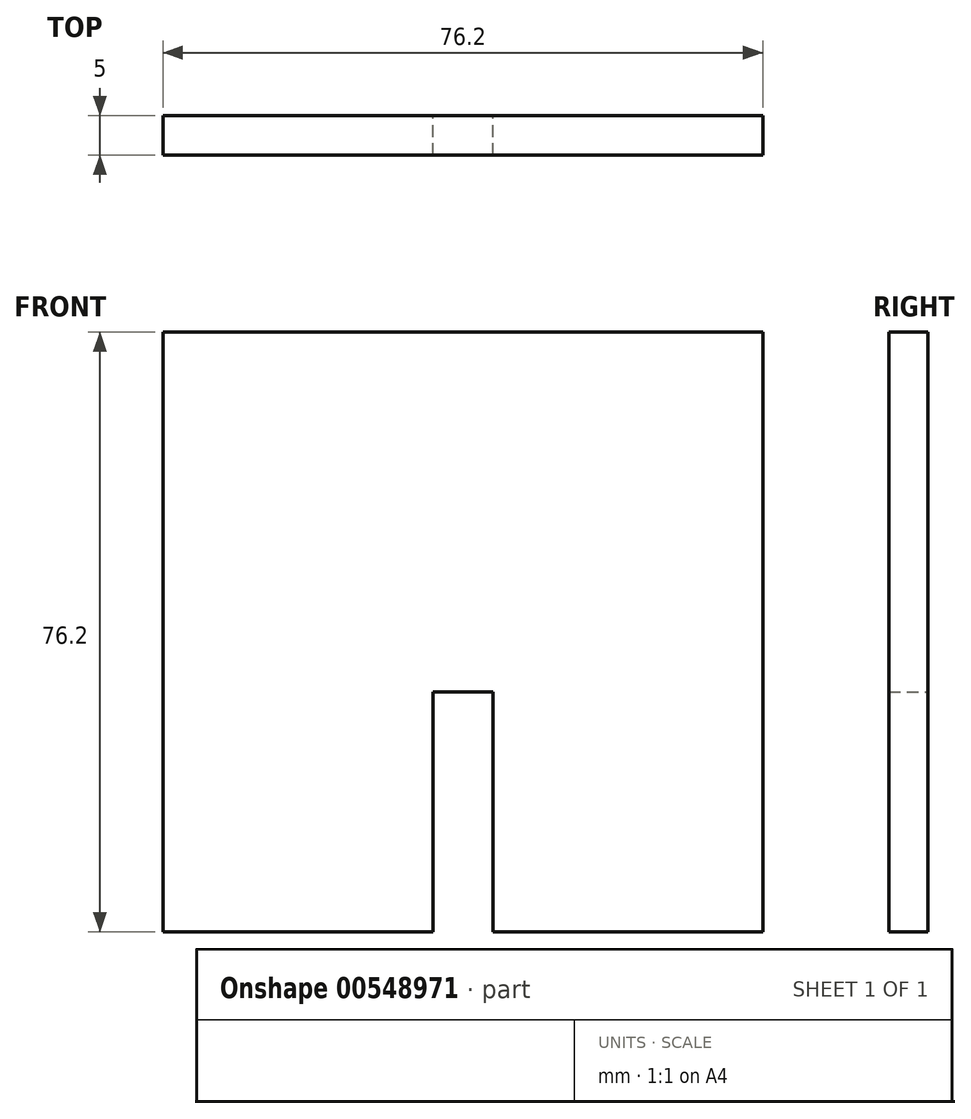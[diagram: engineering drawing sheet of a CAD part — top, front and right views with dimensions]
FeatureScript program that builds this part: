
annotation { "Feature Type Name" : "Feature", "Feature Type Description" : "" }
export const myFeature = defineFeature(function(context is Context, id is Id, definition is map)
    precondition{}
    {
        {
            var Q0;
            Q0=qCreatedBy(makeId("Front.planeOp"),FACE);
            var sketch = newSketch(context, id + "F0", { "sketchPlane" : qUnion([Q0])});
            skLineSegment(sketch, "E0.bottom", {"start": v(-11.31, -25.19) * mm, "end": v(64.89, -25.19) * mm});
            skLineSegment(sketch, "E0.top", {"start": v(-11.31, 51.01) * mm, "end": v(64.89, 51.01) * mm});
            skLineSegment(sketch, "E0.left", {"start": v(-11.31, -25.19) * mm, "end": v(-11.31, 51.01) * mm});
            skLineSegment(sketch, "E0.right", {"start": v(64.89, -25.19) * mm, "end": v(64.89, 51.01) * mm});
            skLineSegment(sketch, "E1.bottom", {"start": v(22.98, -25.19) * mm, "end": v(30.6, -25.19) * mm});
            skLineSegment(sketch, "E1.top", {"start": v(22.98, 5.3) * mm, "end": v(30.6, 5.3) * mm});
            skLineSegment(sketch, "E1.left", {"start": v(22.98, -25.19) * mm, "end": v(22.98, 5.3) * mm});
            skLineSegment(sketch, "E1.right", {"start": v(30.6, -25.19) * mm, "end": v(30.6, 5.3) * mm});
            skSolve(sketch);
        }
        {
            var Q0;
            Q0=makeQuery(id+"F0.imprint","IMPRINT",FACE,{"disambiguationData":[TD([[makeQuery(id+"F0.imprint","IMPRINT",EDGE,{"derivedFrom":sQuery(id+"F0.wireOp",EDGE,"E0.top")}),-1.0]])]});
            extrude(context, id + "F1", {"entities" : qUnion([Q0]), "depth" : 5 * mm, "offsetDistance" : 25.4 * mm});
        }
    });
